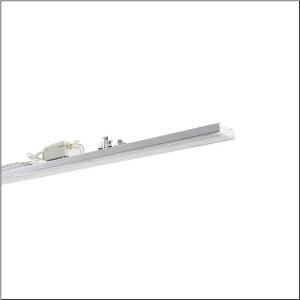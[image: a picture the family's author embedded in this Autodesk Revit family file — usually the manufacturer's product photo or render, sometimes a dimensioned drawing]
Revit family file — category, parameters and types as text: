
# Revit family: licross_r__11_recessed_mo_51te1ecn49xg_60cb
name_source: partatom
category: Lighting Fixtures
units: mm (PartAtom-declared; Revit-internal decimal feet)

## family parameters
Cut with Voids When Loaded = No
Host = Face
Light Source = No
Part Type = Normal
Room Calculation Point = No
Round Connector Dimension = Use Diameter
Shared = No

## types (1)
- --- (1 x LED, 9000 lm, 49.3 W, 4000K)
    Apparent Load = 49 VA
    CIE Flux Codes = 85 95 99 100 100
    Color Rendering = 80
    Color Temperature = 4000K
    Default Elevation = 1800 mm
    Description = Licross® 11 Recessed MO, luminaire insert, of sheet steel, galvanised, coil coated, white, length: 1.500mm, width: 66mm, height: 67mm, LED rated luminous flux: 9.000lm, light colour: 840, control gear: ON/OFF Multilumen, CLOi, with plug, 3-pole, with phase selection, mains connection: 220..240V, AC, 50/60Hz, start of lifetime: 49W, end of service life: 55W, halogen-free wiring, primary light control with lens, of plastic, primary optical cover: cover, of PMMA, light emission: direct distribution, primary light characteristic: symmetric, protection rating (complete): IP54, insulation class (complete): insulation class I (protective earthing), certification: CE, ENEC, VDE, UKCA, protection symbol: D if used in an environment with non-conductive dust loads with corresponding accessories, impact resistance: IK06, permissible ambient temperature for indoor applications: -35..+40°C, corresponds to IFS (International Featured Standards) requirements for safety and quality in the food industry, reducing of maximum allowable ambient temperature of 5°C with ceiling mounting, LABS conformity tested according to VDMA 24364:2018-05, packaging unit: 1 piece
    Height = 58 mm
    Lamp = 1 x LED
    Lamp Light Flux = 9000 lm
    Lamp Power = 49.3 W
    Lamp count = 1
    Length = 1500 mm
    Luminous efficacy = 183 lm/W
    Manufacturer = Siteco
    ModVariant = No
    Model = 51TE1ECN49XG
    Mounting Place = Ceiling
    Mounting Type = Pendant
    Number of Poles = 1
    OnlyDefault = Yes
    Power Factor = 1
    Product Name = Licross® 11 Recessed MO
    Product group = luminaire insert
    ProductGroupID = 901
    Protection Class = Protection class I
    Protection Degree = IP 54
    RLX_Detail_Level = 1
    RLX_Emergency_Light_Flux = 0 lm
    RLX_Emergency_Type = 0
    RLX_Emergency_Type_DB = No
    RlxData = <blob elided: 22421 chars, md5=30ca0cf0>
    Socket = socket
    Standby Power = 0 W
    System Light Flux = 9000 lm
    System Power = 49 W
    Type Comments = factory setting: luminous flux: 100 % | (A | C | E) | 113 mA
    Type Image = l_1296930.jpg
    URL = http://relux.com
    VarID = @adj_053557
    Voltage = 0 V
    Weight = 0.00 kg
    Width = 66 mm

## geometry (parser evidence)
native form markers: Blend x4, Sweep x9
no freeform markers — native parametric forms only
